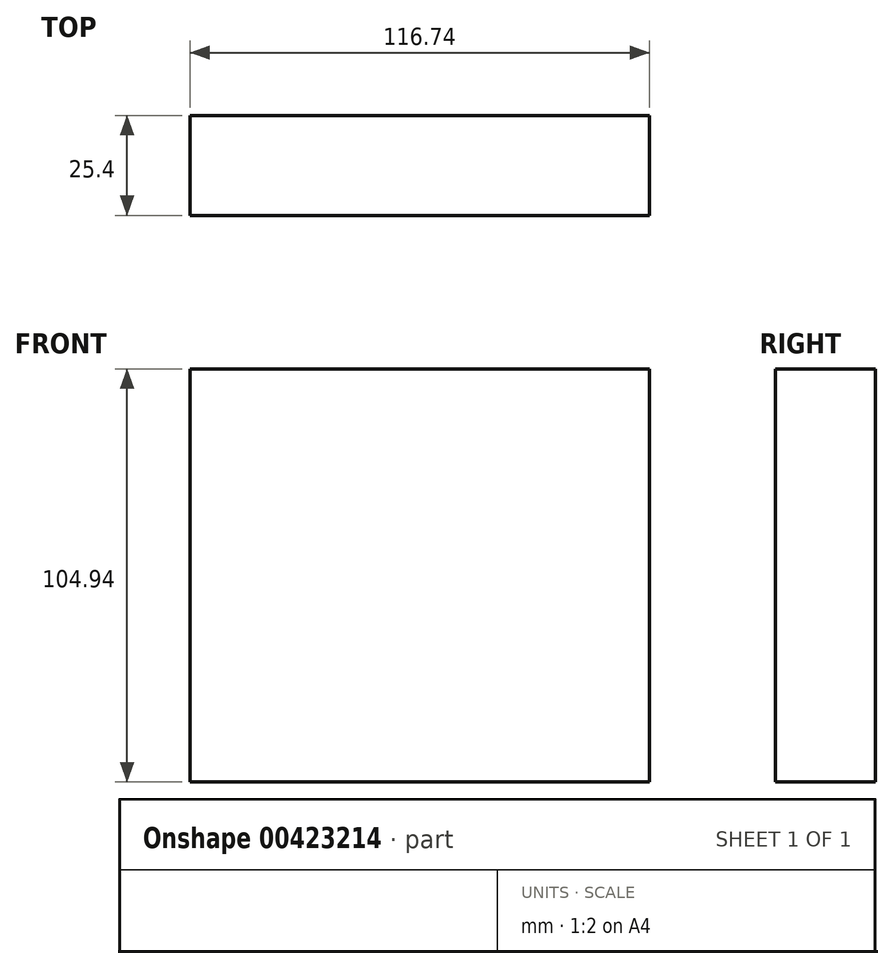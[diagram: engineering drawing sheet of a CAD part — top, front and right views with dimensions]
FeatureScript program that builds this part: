
annotation { "Feature Type Name" : "Feature", "Feature Type Description" : "" }
export const myFeature = defineFeature(function(context is Context, id is Id, definition is map)
    precondition{}
    {
        {
            var Q0;
            Q0=qCreatedBy(makeId("Front.planeOp"),FACE);
            var sketch = newSketch(context, id + "F0", { "sketchPlane" : qUnion([Q0])});
            skLineSegment(sketch, "E0.bottom", {"start": v(-78.7, -34.78) * mm, "end": v(-68.8, -34.78) * mm});
            skLineSegment(sketch, "E0.top", {"start": v(-78.7, -34.25) * mm, "end": v(-68.8, -34.25) * mm});
            skLineSegment(sketch, "E0.left", {"start": v(-78.7, -34.78) * mm, "end": v(-78.7, -34.25) * mm});
            skLineSegment(sketch, "E0.right", {"start": v(-68.8, -34.78) * mm, "end": v(-68.8, -34.25) * mm});
            skLineSegment(sketch, "E1.bottom", {"start": v(37.79, 0) * mm, "end": v(0, 0) * mm});
            skLineSegment(sketch, "E1.top", {"start": v(37.79, 0) * mm, "end": v(0, 0) * mm});
            skLineSegment(sketch, "E1.left", {"start": v(37.79, 0) * mm, "end": v(37.79, 0) * mm});
            skLineSegment(sketch, "E1.right", {"start": v(0, 0) * mm, "end": v(0, 0) * mm});
            skLineSegment(sketch, "E2.top", {"start": v(37.79, 3.85) * mm, "end": v(37.79, 3.85) * mm});
            skLineSegment(sketch, "E2.left", {"start": v(37.79, 0) * mm, "end": v(37.79, 3.85) * mm});
            skLineSegment(sketch, "E2.right", {"start": v(37.79, 0) * mm, "end": v(37.79, 3.85) * mm});
            skLineSegment(sketch, "E3.bottom", {"start": v(37.89, -0.28) * mm, "end": v(-78.85, -0.28) * mm});
            skLineSegment(sketch, "E3.top", {"start": v(37.89, 104.66) * mm, "end": v(-78.85, 104.66) * mm});
            skLineSegment(sketch, "E3.left", {"start": v(37.89, -0.28) * mm, "end": v(37.89, 104.66) * mm});
            skLineSegment(sketch, "E3.right", {"start": v(-78.85, -0.28) * mm, "end": v(-78.85, 104.66) * mm});
            skSolve(sketch);
        }
        {
            var Q0;
            Q0=makeQuery(id+"F0.imprint","IMPRINT",FACE,{"disambiguationData":[TD([[makeQuery(id+"F0.imprint","IMPRINT",EDGE,{"derivedFrom":sQuery(id+"F0.wireOp",EDGE,"E3.bottom")}),-1.0]])]});
            extrude(context, id + "F1", {"entities" : qUnion([Q0]), "depth" : 25.4 * mm});
        }
    });
